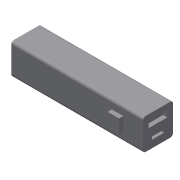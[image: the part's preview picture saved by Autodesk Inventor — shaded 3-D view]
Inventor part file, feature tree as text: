
AUTODESK INVENTOR PART (.ipt)
format: ipt  version: 2019.4 (Build 234330000, 330)  size: 112,640 bytes
history: native  units: mm
features: extrude x3, sketch x3, projected_geometry x1
ambient origin geometry x8: Origin, YZ Plane, XZ Plane, XY Plane, X Axis, Y Axis, Z Axis, Center Point
bodies: Solid1 (feature_tree)
feature tree (7):
  extrude  "Extrusion1"  Depth=21.46mm
  extrude  "Extrusion2"  Depth=94.0mm TaperAngle=0.0deg
  extrude  "Extrusion3"  Depth=8.2mm
  sketch  "Sketch1"  dims[d0=22.22mm d1=21.46mm]
  sketch  "Sketch2"  dims[d2=2.0mm d3=94.0mm d4=0.0mm]
  sketch  "Sketch3"  dims[d5=3.0mm d6=0.0mm d7=8.2mm d8=10.0mm d9=14.0mm d10=3.0mm d11=0.0mm]
  projected_geometry  "Projected Loop1"
